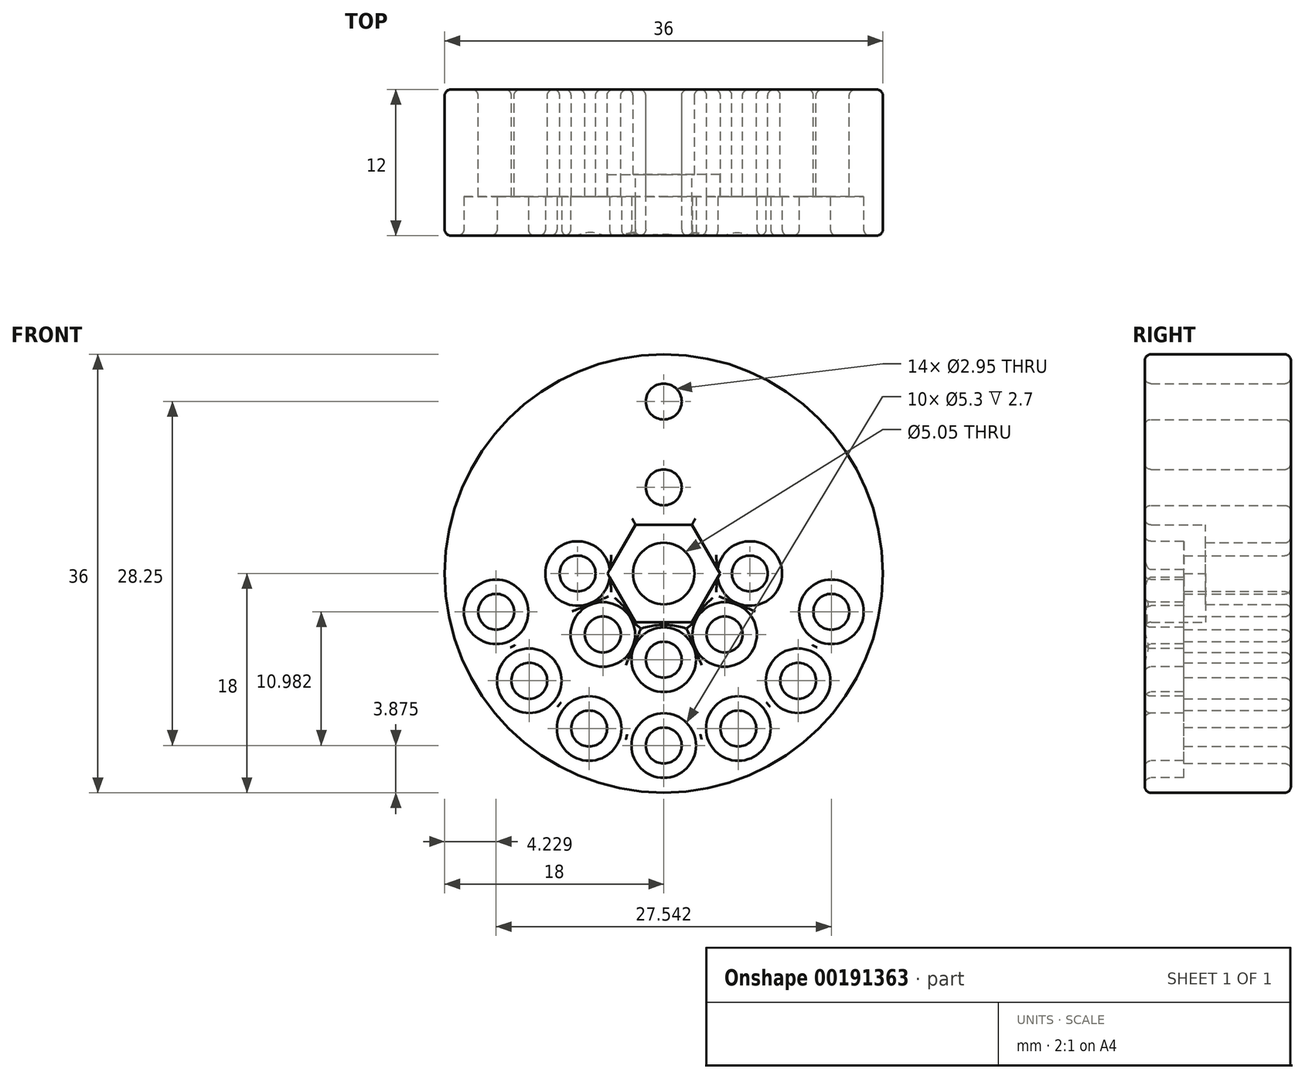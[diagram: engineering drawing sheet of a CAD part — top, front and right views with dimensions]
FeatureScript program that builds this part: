
annotation { "Feature Type Name" : "Feature", "Feature Type Description" : "" }
export const myFeature = defineFeature(function(context is Context, id is Id, definition is map)
    precondition{}
    {
        {
            assignVariable(context, id + "F0", {"name" : "nut_depth_mm", "anyValue" : 5});
        }
        {
            assignVariable(context, id + "F1", {"name" : "flywheel_depth_mm", "anyValue" : 12});
        }
        {
            var Q0;
            Q0=qCreatedBy(makeId("Front.planeOp"),FACE);
            var sketch = newSketch(context, id + "F2", { "sketchPlane" : qUnion([Q0])});
            skCircle(sketch, "E0", {"center": v(0, 0) * mm, "radius": 18 * mm});
            skCircle(sketch, "E1", {"center": v(0, 14.13) * mm, "radius": 1.48 * mm});
            skCircle(sketch, "E2.1.0", {"center": v(-6.13, 12.73) * mm, "radius": 1.48 * mm});
            skCircle(sketch, "E2.2.0", {"center": v(-11.04, 8.8) * mm, "radius": 1.47 * mm});
            skCircle(sketch, "E3.1.3.0", {"center": v(-13.77, 3.14) * mm, "radius": 1.48 * mm});
            skCircle(sketch, "E3.1.4.0", {"center": v(-13.77, -3.14) * mm, "radius": 1.48 * mm});
            skCircle(sketch, "E3.1.5.0", {"center": v(-11.04, -8.8) * mm, "radius": 1.47 * mm});
            skCircle(sketch, "E3.1.6.0", {"center": v(-6.13, -12.73) * mm, "radius": 1.47 * mm});
            skCircle(sketch, "E3.1.7.0", {"center": v(0, -14.13) * mm, "radius": 1.48 * mm});
            skCircle(sketch, "E3.1.8.0", {"center": v(6.13, -12.73) * mm, "radius": 1.47 * mm});
            skCircle(sketch, "E3.1.9.0", {"center": v(11.04, -8.8) * mm, "radius": 1.48 * mm});
            skCircle(sketch, "E3.1.10.0", {"center": v(13.77, -3.14) * mm, "radius": 1.48 * mm});
            skCircle(sketch, "E3.1.11.0", {"center": v(13.77, 3.14) * mm, "radius": 1.48 * mm});
            skCircle(sketch, "E3.1.12.0", {"center": v(11.04, 8.8) * mm, "radius": 1.48 * mm});
            skCircle(sketch, "E3.1.13.0", {"center": v(6.13, 12.73) * mm, "radius": 1.48 * mm});
            skCircle(sketch, "E4", {"center": v(0, 0) * mm, "radius": 2.5 * mm, "construction": true});
            skCircle(sketch, "E5", {"center": v(0, 0) * mm, "radius": 5.75 * mm, "construction": true});
            skCircle(sketch, "E6", {"center": v(0, 7.08) * mm, "radius": 1.48 * mm});
            skCircle(sketch, "E7.1.0", {"center": v(-5, 5) * mm, "radius": 1.48 * mm});
            skCircle(sketch, "E7.2.0", {"center": v(-7.08, 0) * mm, "radius": 1.48 * mm});
            skCircle(sketch, "E8.1.3.0", {"center": v(-5, -5) * mm, "radius": 1.48 * mm});
            skCircle(sketch, "E8.1.4.0", {"center": v(0, -7.08) * mm, "radius": 1.48 * mm});
            skCircle(sketch, "E8.1.5.0", {"center": v(5, -5) * mm, "radius": 1.48 * mm});
            skCircle(sketch, "E8.1.6.0", {"center": v(7.08, 0) * mm, "radius": 1.48 * mm});
            skCircle(sketch, "E8.1.7.0", {"center": v(5, 5) * mm, "radius": 1.48 * mm});
            skCircle(sketch, "E9.cCircle", {"center": v(0, 0) * mm, "radius": 4 * mm, "construction": true});
            skLineSegment(sketch, "E9.0", {"start": v(-2.3, 4) * mm, "end": v(2.3, 4) * mm});
            skLineSegment(sketch, "E9.1", {"start": v(2.3, 4) * mm, "end": v(4.62, 0) * mm});
            skLineSegment(sketch, "E9.2", {"start": v(4.62, 0) * mm, "end": v(2.3, -4) * mm});
            skLineSegment(sketch, "E9.3", {"start": v(2.3, -4) * mm, "end": v(-2.3, -4) * mm});
            skLineSegment(sketch, "E9.4", {"start": v(-2.3, -4) * mm, "end": v(-4.62, 0) * mm});
            skLineSegment(sketch, "E9.5", {"start": v(-4.62, 0) * mm, "end": v(-2.3, 4) * mm});
            skPoint(sketch, "E9.0.midPoint", {"position": v(0, 4) * mm});
            skSolve(sketch);
        }
        {
            var Q0;
            {var subQ0=sQuery(id+"F2.wireOp",EDGE,"E9.3");var subQ1=sQuery(id+"F2.wireOp",EDGE,"E5");var subQ2=makeQuery(id+"F2.imprint","INTERSECT",VERTEX,{"disambiguationData":[OD(0.0)],"derivedFrom":[subQ1,subQ0]});Q0=makeQuery(id+"F2.imprint","IMPRINT",FACE,{"disambiguationData":[TD([[makeQuery(id+"F2.imprint","IMPRINT",EDGE,{"disambiguationData":[TD([[subQ2,-1.0]])],"derivedFrom":subQ1}),1.0]])]});}
            var Q1;
            {var subQ0=sQuery(id+"F2.wireOp",EDGE,"E9.2");var subQ1=sQuery(id+"F2.wireOp",EDGE,"E5");var subQ2=makeQuery(id+"F2.imprint","INTERSECT",VERTEX,{"disambiguationData":[OD(0.0)],"derivedFrom":[subQ1,subQ0]});Q1=makeQuery(id+"F2.imprint","IMPRINT",FACE,{"disambiguationData":[TD([[makeQuery(id+"F2.imprint","IMPRINT",EDGE,{"disambiguationData":[TD([[subQ2,-1.0]])],"derivedFrom":subQ1}),1.0]])]});}
            var Q2;
            {var subQ0=sQuery(id+"F2.wireOp",EDGE,"E9.4");var subQ1=sQuery(id+"F2.wireOp",EDGE,"E5");var subQ2=makeQuery(id+"F2.imprint","INTERSECT",VERTEX,{"disambiguationData":[OD(0.0)],"derivedFrom":[subQ1,subQ0]});Q2=makeQuery(id+"F2.imprint","IMPRINT",FACE,{"disambiguationData":[TD([[makeQuery(id+"F2.imprint","IMPRINT",EDGE,{"disambiguationData":[TD([[subQ2,-1.0]])],"derivedFrom":subQ1}),1.0]])]});}
            var Q3;
            {var subQ0=sQuery(id+"F2.wireOp",EDGE,"E9.0");var subQ1=sQuery(id+"F2.wireOp",EDGE,"E5");var subQ2=makeQuery(id+"F2.imprint","INTERSECT",VERTEX,{"disambiguationData":[OD(0.0)],"derivedFrom":[subQ1,subQ0]});Q3=makeQuery(id+"F2.imprint","IMPRINT",FACE,{"disambiguationData":[TD([[makeQuery(id+"F2.imprint","IMPRINT",EDGE,{"disambiguationData":[TD([[subQ2,-1.0]])],"derivedFrom":subQ1}),1.0]])]});}
            var Q4;
            {var subQ0=sQuery(id+"F2.wireOp",EDGE,"E9.1");var subQ1=sQuery(id+"F2.wireOp",EDGE,"E5");var subQ2=makeQuery(id+"F2.imprint","INTERSECT",VERTEX,{"disambiguationData":[OD(0.0)],"derivedFrom":[subQ1,subQ0]});Q4=makeQuery(id+"F2.imprint","IMPRINT",FACE,{"disambiguationData":[TD([[makeQuery(id+"F2.imprint","IMPRINT",EDGE,{"disambiguationData":[TD([[subQ2,1.0]])],"derivedFrom":subQ1}),1.0]])]});}
            var Q5;
            Q5=makeQuery(id+"F2.imprint","IMPRINT",FACE,{"disambiguationData":[TD([[makeQuery(id+"F2.imprint","IMPRINT",EDGE,{"derivedFrom":sQuery(id+"F2.wireOp",EDGE,"E0")}),1.0]])]});
            var Q6;
            {var subQ0=sQuery(id+"F2.wireOp",EDGE,"E9.5");var subQ1=sQuery(id+"F2.wireOp",EDGE,"E5");var subQ2=makeQuery(id+"F2.imprint","INTERSECT",VERTEX,{"disambiguationData":[OD(0.0)],"derivedFrom":[subQ1,subQ0]});Q6=makeQuery(id+"F2.imprint","IMPRINT",FACE,{"disambiguationData":[TD([[makeQuery(id+"F2.imprint","IMPRINT",EDGE,{"disambiguationData":[TD([[subQ2,-1.0]])],"derivedFrom":subQ1}),1.0]])]});}
            var Q7;
            Q7=makeQuery(id+"F2.imprint","IMPRINT",FACE,{"disambiguationData":[TD([[makeQuery(id+"F2.imprint","IMPRINT",EDGE,{"derivedFrom":sQuery(id+"F2.wireOp",EDGE,"E3.1.13.0")}),1.0]])]});
            var Q8;
            Q8=makeQuery(id+"F2.imprint","IMPRINT",FACE,{"disambiguationData":[TD([[makeQuery(id+"F2.imprint","IMPRINT",EDGE,{"derivedFrom":sQuery(id+"F2.wireOp",EDGE,"E3.1.12.0")}),1.0]])]});
            var Q9;
            Q9=makeQuery(id+"F2.imprint","IMPRINT",FACE,{"disambiguationData":[TD([[makeQuery(id+"F2.imprint","IMPRINT",EDGE,{"derivedFrom":sQuery(id+"F2.wireOp",EDGE,"E3.1.11.0")}),1.0]])]});
            var Q10;
            Q10=makeQuery(id+"F2.imprint","IMPRINT",FACE,{"disambiguationData":[TD([[makeQuery(id+"F2.imprint","IMPRINT",EDGE,{"derivedFrom":sQuery(id+"F2.wireOp",EDGE,"E8.1.7.0")}),1.0]])]});
            var Q11;
            Q11=makeQuery(id+"F2.imprint","IMPRINT",FACE,{"disambiguationData":[TD([[makeQuery(id+"F2.imprint","IMPRINT",EDGE,{"derivedFrom":sQuery(id+"F2.wireOp",EDGE,"E7.1.0")}),1.0]])]});
            var Q12;
            Q12=makeQuery(id+"F2.imprint","IMPRINT",FACE,{"disambiguationData":[TD([[makeQuery(id+"F2.imprint","IMPRINT",EDGE,{"derivedFrom":sQuery(id+"F2.wireOp",EDGE,"E2.1.0")}),1.0]])]});
            var Q13;
            Q13=makeQuery(id+"F2.imprint","IMPRINT",FACE,{"disambiguationData":[TD([[makeQuery(id+"F2.imprint","IMPRINT",EDGE,{"derivedFrom":sQuery(id+"F2.wireOp",EDGE,"E2.2.0")}),1.0]])]});
            var Q14;
            Q14=makeQuery(id+"F2.imprint","IMPRINT",FACE,{"disambiguationData":[TD([[makeQuery(id+"F2.imprint","IMPRINT",EDGE,{"derivedFrom":sQuery(id+"F2.wireOp",EDGE,"E3.1.3.0")}),1.0]])]});
            extrude(context, id + "F3", {"entities" : qUnion([Q0, Q1, Q2, Q3, Q4, Q5, Q6, Q7, Q8, Q9, Q10, Q11, Q12, Q13, Q14]), "depth" : (getVariable(context, 'flywheel_depth_mm')) * mm});
        }
        {
            var Q0;
            Q0=makeQuery(id+"F2.imprint","IMPRINT",FACE,{"disambiguationData":[TD([[makeQuery(id+"F2.imprint","IMPRINT",EDGE,{"derivedFrom":sQuery(id+"F2.wireOp",EDGE,"E9.0")}),-1.0]])]});
            extrude(context, id + "F4", {"entities" : qUnion([Q0]), "operationType" : NewBodyOperationType.ADD, "depth" : (getVariable(context, 'flywheel_depth_mm') - getVariable(context, 'nut_depth_mm')) * mm});
        }
        {
            var Q0;
            Q0=sQuery(id+"F2.wireOp",VERTEX,"E0.center");
            var Q1;
            Q1=makeQuery(id+"F3.opExtrude","SWEPT_BODY",BODY,{"disambiguationData":[OSD([sQuery(id+"F2.wireOp",EDGE,"E0"),sQuery(id+"F2.wireOp",EDGE,"E1"),sQuery(id+"F2.wireOp",EDGE,"E2.1.0"),sQuery(id+"F2.wireOp",EDGE,"E2.2.0"),sQuery(id+"F2.wireOp",EDGE,"E3.1.3.0"),sQuery(id+"F2.wireOp",EDGE,"E3.1.4.0"),sQuery(id+"F2.wireOp",EDGE,"E3.1.5.0"),sQuery(id+"F2.wireOp",EDGE,"E3.1.6.0"),sQuery(id+"F2.wireOp",EDGE,"E3.1.7.0"),sQuery(id+"F2.wireOp",EDGE,"E3.1.8.0"),sQuery(id+"F2.wireOp",EDGE,"E3.1.9.0"),sQuery(id+"F2.wireOp",EDGE,"E3.1.10.0"),sQuery(id+"F2.wireOp",EDGE,"E3.1.11.0"),sQuery(id+"F2.wireOp",EDGE,"E3.1.12.0"),sQuery(id+"F2.wireOp",EDGE,"E3.1.13.0"),sQuery(id+"F2.wireOp",EDGE,"E3.1.14.0"),sQuery(id+"F2.wireOp",EDGE,"E3.1.15.0"),sQuery(id+"F2.wireOp",EDGE,"E6"),sQuery(id+"F2.wireOp",EDGE,"E7.1.0"),sQuery(id+"F2.wireOp",EDGE,"E7.2.0"),sQuery(id+"F2.wireOp",EDGE,"E8.1.3.0"),sQuery(id+"F2.wireOp",EDGE,"E8.1.4.0"),sQuery(id+"F2.wireOp",EDGE,"E8.1.5.0"),sQuery(id+"F2.wireOp",EDGE,"E8.1.6.0"),sQuery(id+"F2.wireOp",EDGE,"E8.1.7.0"),sQuery(id+"F2.wireOp",EDGE,"E9.0"),sQuery(id+"F2.wireOp",EDGE,"E9.1"),sQuery(id+"F2.wireOp",EDGE,"E9.2"),sQuery(id+"F2.wireOp",EDGE,"E9.3"),sQuery(id+"F2.wireOp",EDGE,"E9.4"),sQuery(id+"F2.wireOp",EDGE,"E9.5")])]});
            hole(context, id + "F5", {"style" : HoleStyle.SIMPLE, "endStyle" : HoleEndStyle.THROUGH, "oppositeDirection" : true, "holeDiameter" : 5.05 * mm, "tappedDepth" : 12 * mm, "tapClearance" : 3, "locations" : qUnion([Q0]), "scope" : qUnion([Q1])});
        }
        {
            var Q0;
            Q0=makeQuery(id+"F3.opExtrude","CAP_FACE",FACE,{"disambiguationData":[OSD([sQuery(id+"F2.wireOp",EDGE,"E0"),sQuery(id+"F2.wireOp",EDGE,"E1"),sQuery(id+"F2.wireOp",EDGE,"E2.1.0"),sQuery(id+"F2.wireOp",EDGE,"E2.2.0"),sQuery(id+"F2.wireOp",EDGE,"E3.1.3.0"),sQuery(id+"F2.wireOp",EDGE,"E3.1.4.0"),sQuery(id+"F2.wireOp",EDGE,"E3.1.5.0"),sQuery(id+"F2.wireOp",EDGE,"E3.1.6.0"),sQuery(id+"F2.wireOp",EDGE,"E3.1.7.0"),sQuery(id+"F2.wireOp",EDGE,"E3.1.8.0"),sQuery(id+"F2.wireOp",EDGE,"E3.1.9.0"),sQuery(id+"F2.wireOp",EDGE,"E3.1.10.0"),sQuery(id+"F2.wireOp",EDGE,"E3.1.11.0"),sQuery(id+"F2.wireOp",EDGE,"E3.1.12.0"),sQuery(id+"F2.wireOp",EDGE,"E3.1.13.0"),sQuery(id+"F2.wireOp",EDGE,"E3.1.14.0"),sQuery(id+"F2.wireOp",EDGE,"E3.1.15.0"),sQuery(id+"F2.wireOp",EDGE,"E6"),sQuery(id+"F2.wireOp",EDGE,"E7.1.0"),sQuery(id+"F2.wireOp",EDGE,"E7.2.0"),sQuery(id+"F2.wireOp",EDGE,"E8.1.3.0"),sQuery(id+"F2.wireOp",EDGE,"E8.1.4.0"),sQuery(id+"F2.wireOp",EDGE,"E8.1.5.0"),sQuery(id+"F2.wireOp",EDGE,"E8.1.6.0"),sQuery(id+"F2.wireOp",EDGE,"E8.1.7.0"),sQuery(id+"F2.wireOp",EDGE,"E9.0"),sQuery(id+"F2.wireOp",EDGE,"E9.1"),sQuery(id+"F2.wireOp",EDGE,"E9.2"),sQuery(id+"F2.wireOp",EDGE,"E9.3"),sQuery(id+"F2.wireOp",EDGE,"E9.4"),sQuery(id+"F2.wireOp",EDGE,"E9.5")])],"isStart":false});
            var sketch = newSketch(context, id + "F6", { "sketchPlane" : qUnion([Q0])});
            skCircle(sketch, "E10", {"center": v(-7.08, 0) * mm, "radius": 2.65 * mm});
            skCircle(sketch, "E11", {"center": v(-13.77, -3.14) * mm, "radius": 2.65 * mm});
            skCircle(sketch, "E12", {"center": v(-11.04, -8.8) * mm, "radius": 2.65 * mm});
            skCircle(sketch, "E13", {"center": v(-5, -5) * mm, "radius": 2.65 * mm});
            skCircle(sketch, "E14", {"center": v(-6.13, -12.73) * mm, "radius": 2.65 * mm});
            skCircle(sketch, "E15", {"center": v(0, -14.13) * mm, "radius": 2.65 * mm});
            skCircle(sketch, "E16", {"center": v(6.13, -12.73) * mm, "radius": 2.65 * mm});
            skCircle(sketch, "E17", {"center": v(0, -7.08) * mm, "radius": 2.65 * mm});
            skCircle(sketch, "E18", {"center": v(11.04, -8.8) * mm, "radius": 2.65 * mm});
            skCircle(sketch, "E19", {"center": v(13.77, -3.14) * mm, "radius": 2.65 * mm});
            skCircle(sketch, "E20", {"center": v(5, -5) * mm, "radius": 2.65 * mm});
            skCircle(sketch, "E21", {"center": v(7.08, 0) * mm, "radius": 2.65 * mm});
            skSolve(sketch);
        }
        {
            var Q0;
            Q0=makeQuery(id+"F6.imprint","IMPRINT",FACE,{"disambiguationData":[TD([[makeQuery(id+"F6.imprint","IMPRINT",EDGE,{"derivedFrom":sQuery(id+"F6.wireOp",EDGE,"E13")}),1.0]])]});
            var Q1;
            Q1=makeQuery(id+"F6.imprint","IMPRINT",FACE,{"disambiguationData":[TD([[makeQuery(id+"F6.imprint","IMPRINT",EDGE,{"derivedFrom":makeQuery(id+"F3.opExtrude","CAP_EDGE",EDGE,{"disambiguationData":[OSD([sQuery(id+"F2.wireOp",EDGE,"E7.2.0")])],"isStart":false})}),-1.0]])]});
            var Q2;
            Q2=makeQuery(id+"F6.imprint","IMPRINT",FACE,{"disambiguationData":[TD([[makeQuery(id+"F6.imprint","IMPRINT",EDGE,{"derivedFrom":sQuery(id+"F6.wireOp",EDGE,"E11")}),1.0]])]});
            var Q3;
            Q3=makeQuery(id+"F6.imprint","IMPRINT",FACE,{"disambiguationData":[TD([[makeQuery(id+"F6.imprint","IMPRINT",EDGE,{"derivedFrom":sQuery(id+"F6.wireOp",EDGE,"E12")}),1.0]])]});
            var Q4;
            Q4=makeQuery(id+"F6.imprint","IMPRINT",FACE,{"disambiguationData":[TD([[makeQuery(id+"F6.imprint","IMPRINT",EDGE,{"derivedFrom":sQuery(id+"F6.wireOp",EDGE,"E14")}),1.0]])]});
            var Q5;
            Q5=makeQuery(id+"F6.imprint","IMPRINT",FACE,{"disambiguationData":[TD([[makeQuery(id+"F6.imprint","IMPRINT",EDGE,{"derivedFrom":sQuery(id+"F6.wireOp",EDGE,"E17")}),1.0]])]});
            var Q6;
            Q6=makeQuery(id+"F6.imprint","IMPRINT",FACE,{"disambiguationData":[TD([[makeQuery(id+"F6.imprint","IMPRINT",EDGE,{"derivedFrom":sQuery(id+"F6.wireOp",EDGE,"E20")}),1.0]])]});
            var Q7;
            Q7=makeQuery(id+"F6.imprint","IMPRINT",FACE,{"disambiguationData":[TD([[makeQuery(id+"F6.imprint","IMPRINT",EDGE,{"derivedFrom":makeQuery(id+"F3.opExtrude","CAP_EDGE",EDGE,{"disambiguationData":[OSD([sQuery(id+"F2.wireOp",EDGE,"E8.1.6.0")])],"isStart":false})}),-1.0]])]});
            var Q8;
            Q8=makeQuery(id+"F6.imprint","IMPRINT",FACE,{"disambiguationData":[TD([[makeQuery(id+"F6.imprint","IMPRINT",EDGE,{"derivedFrom":sQuery(id+"F6.wireOp",EDGE,"E19")}),1.0]])]});
            var Q9;
            Q9=makeQuery(id+"F6.imprint","IMPRINT",FACE,{"disambiguationData":[TD([[makeQuery(id+"F6.imprint","IMPRINT",EDGE,{"derivedFrom":sQuery(id+"F6.wireOp",EDGE,"E18")}),1.0]])]});
            var Q10;
            Q10=makeQuery(id+"F6.imprint","IMPRINT",FACE,{"disambiguationData":[TD([[makeQuery(id+"F6.imprint","IMPRINT",EDGE,{"derivedFrom":sQuery(id+"F6.wireOp",EDGE,"E16")}),1.0]])]});
            var Q11;
            Q11=makeQuery(id+"F6.imprint","IMPRINT",FACE,{"disambiguationData":[TD([[makeQuery(id+"F6.imprint","IMPRINT",EDGE,{"derivedFrom":sQuery(id+"F6.wireOp",EDGE,"E15")}),1.0]])]});
            extrude(context, id + "F7", {"entities" : qUnion([Q0, Q1, Q2, Q3, Q4, Q5, Q6, Q7, Q8, Q9, Q10, Q11]), "operationType" : NewBodyOperationType.REMOVE, "oppositeDirection" : true, "depth" : 3.2 * mm});
        }
        {
            var Q0;
            Q0=makeQuery(id+"F3.opExtrude","CAP_EDGE",EDGE,{"disambiguationData":[OSD([sQuery(id+"F2.wireOp",EDGE,"E9.0")])],"isStart":false});
            var Q1;
            Q1=makeQuery(id+"F3.opExtrude","CAP_EDGE",EDGE,{"disambiguationData":[OSD([sQuery(id+"F2.wireOp",EDGE,"E9.1")])],"isStart":false});
            var Q2;
            Q2=makeQuery(id+"F3.opExtrude","CAP_EDGE",EDGE,{"disambiguationData":[OSD([sQuery(id+"F2.wireOp",EDGE,"E9.2")])],"isStart":false});
            var Q3;
            Q3=makeQuery(id+"F3.opExtrude","CAP_EDGE",EDGE,{"disambiguationData":[OSD([sQuery(id+"F2.wireOp",EDGE,"E9.3")])],"isStart":false});
            var Q4;
            Q4=makeQuery(id+"F3.opExtrude","CAP_EDGE",EDGE,{"disambiguationData":[OSD([sQuery(id+"F2.wireOp",EDGE,"E9.4")])],"isStart":false});
            var Q5;
            Q5=makeQuery(id+"F3.opExtrude","CAP_EDGE",EDGE,{"disambiguationData":[OSD([sQuery(id+"F2.wireOp",EDGE,"E9.5")])],"isStart":false});
            var Q6;
            Q6=makeQuery(id+"F3.opExtrude","CAP_EDGE",EDGE,{"disambiguationData":[OSD([sQuery(id+"F2.wireOp",EDGE,"E0")])],"isStart":false});
            var Q7;
            Q7=makeQuery(id+"F3.opExtrude","CAP_EDGE",EDGE,{"disambiguationData":[OSD([sQuery(id+"F2.wireOp",EDGE,"E0")])],"isStart":true});
            var Q8;
            Q8=makeQuery(id+"F4.opExtrude","CAP_EDGE",EDGE,{"disambiguationData":[OSD([sQuery(id+"F2.wireOp",EDGE,"E4")])],"isStart":true});
            var Q9;
            Q9=makeQuery(id+"F4.opExtrude","CAP_EDGE",EDGE,{"disambiguationData":[OSD([sQuery(id+"F2.wireOp",EDGE,"E4")])],"isStart":false});
            var Q10;
            Q10=makeQuery(id+"F3.opExtrude","CAP_FACE",FACE,{"disambiguationData":[OSD([sQuery(id+"F2.wireOp",EDGE,"E0"),sQuery(id+"F2.wireOp",EDGE,"E1"),sQuery(id+"F2.wireOp",EDGE,"E2.1.0"),sQuery(id+"F2.wireOp",EDGE,"E2.2.0"),sQuery(id+"F2.wireOp",EDGE,"E3.1.3.0"),sQuery(id+"F2.wireOp",EDGE,"E3.1.4.0"),sQuery(id+"F2.wireOp",EDGE,"E3.1.5.0"),sQuery(id+"F2.wireOp",EDGE,"E3.1.6.0"),sQuery(id+"F2.wireOp",EDGE,"E3.1.7.0"),sQuery(id+"F2.wireOp",EDGE,"E3.1.8.0"),sQuery(id+"F2.wireOp",EDGE,"E3.1.9.0"),sQuery(id+"F2.wireOp",EDGE,"E3.1.10.0"),sQuery(id+"F2.wireOp",EDGE,"E3.1.11.0"),sQuery(id+"F2.wireOp",EDGE,"E3.1.12.0"),sQuery(id+"F2.wireOp",EDGE,"E3.1.13.0"),sQuery(id+"F2.wireOp",EDGE,"E3.1.14.0"),sQuery(id+"F2.wireOp",EDGE,"E3.1.15.0"),sQuery(id+"F2.wireOp",EDGE,"E6"),sQuery(id+"F2.wireOp",EDGE,"E7.1.0"),sQuery(id+"F2.wireOp",EDGE,"E7.2.0"),sQuery(id+"F2.wireOp",EDGE,"E8.1.3.0"),sQuery(id+"F2.wireOp",EDGE,"E8.1.4.0"),sQuery(id+"F2.wireOp",EDGE,"E8.1.5.0"),sQuery(id+"F2.wireOp",EDGE,"E8.1.6.0"),sQuery(id+"F2.wireOp",EDGE,"E8.1.7.0"),sQuery(id+"F2.wireOp",EDGE,"E9.0"),sQuery(id+"F2.wireOp",EDGE,"E9.1"),sQuery(id+"F2.wireOp",EDGE,"E9.2"),sQuery(id+"F2.wireOp",EDGE,"E9.3"),sQuery(id+"F2.wireOp",EDGE,"E9.4"),sQuery(id+"F2.wireOp",EDGE,"E9.5")])],"isStart":false});
            var Q11;
            {var subQ0=sQuery(id+"F2.wireOp",EDGE,"E9.5");var subQ1=sQuery(id+"F2.wireOp",EDGE,"E9.4");var subQ2=sQuery(id+"F2.wireOp",EDGE,"E9.3");var subQ3=sQuery(id+"F2.wireOp",EDGE,"E9.2");var subQ4=sQuery(id+"F2.wireOp",EDGE,"E9.1");var subQ5=sQuery(id+"F2.wireOp",EDGE,"E9.0");Q11=makeQuery(id+"F4.boolean.opBoolean","MERGE",FACE,{"derivedFrom":[makeQuery(id+"F3.opExtrude","CAP_FACE",FACE,{"disambiguationData":[OSD([sQuery(id+"F2.wireOp",EDGE,"E0"),sQuery(id+"F2.wireOp",EDGE,"E1"),sQuery(id+"F2.wireOp",EDGE,"E2.1.0"),sQuery(id+"F2.wireOp",EDGE,"E2.2.0"),sQuery(id+"F2.wireOp",EDGE,"E3.1.3.0"),sQuery(id+"F2.wireOp",EDGE,"E3.1.4.0"),sQuery(id+"F2.wireOp",EDGE,"E3.1.5.0"),sQuery(id+"F2.wireOp",EDGE,"E3.1.6.0"),sQuery(id+"F2.wireOp",EDGE,"E3.1.7.0"),sQuery(id+"F2.wireOp",EDGE,"E3.1.8.0"),sQuery(id+"F2.wireOp",EDGE,"E3.1.9.0"),sQuery(id+"F2.wireOp",EDGE,"E3.1.10.0"),sQuery(id+"F2.wireOp",EDGE,"E3.1.11.0"),sQuery(id+"F2.wireOp",EDGE,"E3.1.12.0"),sQuery(id+"F2.wireOp",EDGE,"E3.1.13.0"),sQuery(id+"F2.wireOp",EDGE,"E3.1.14.0"),sQuery(id+"F2.wireOp",EDGE,"E3.1.15.0"),sQuery(id+"F2.wireOp",EDGE,"E6"),sQuery(id+"F2.wireOp",EDGE,"E7.1.0"),sQuery(id+"F2.wireOp",EDGE,"E7.2.0"),sQuery(id+"F2.wireOp",EDGE,"E8.1.3.0"),sQuery(id+"F2.wireOp",EDGE,"E8.1.4.0"),sQuery(id+"F2.wireOp",EDGE,"E8.1.5.0"),sQuery(id+"F2.wireOp",EDGE,"E8.1.6.0"),sQuery(id+"F2.wireOp",EDGE,"E8.1.7.0"),subQ5,subQ4,subQ3,subQ2,subQ1,subQ0])],"isStart":true}),makeQuery(id+"F4.opExtrude","CAP_FACE",FACE,{"disambiguationData":[OSD([sQuery(id+"F2.wireOp",EDGE,"E4"),subQ5,subQ4,subQ3,subQ2,subQ1,subQ0])],"isStart":true})]});}
            var Q12;
            Q12=makeQuery(id+"F5.hole-0.boolean.opBoolean","INTERSECT",EDGE,{"derivedFrom":[makeQuery(id+"F4.opExtrude","CAP_FACE",FACE,{"disambiguationData":[OSD([sQuery(id+"F2.wireOp",EDGE,"E9.0"),sQuery(id+"F2.wireOp",EDGE,"E9.1"),sQuery(id+"F2.wireOp",EDGE,"E9.2"),sQuery(id+"F2.wireOp",EDGE,"E9.3"),sQuery(id+"F2.wireOp",EDGE,"E9.4"),sQuery(id+"F2.wireOp",EDGE,"E9.5")])],"isStart":false}),makeQuery(id+"F5.hole-0.opRevolve","SWEPT_FACE",FACE,{"disambiguationData":[OSD([sQuery(id+"F5.hole-0.sketch.wireOp",EDGE,"core_line_2")])]})]});
            fillet(context, id + "F8", {"entities" : qUnion([Q0, Q1, Q2, Q3, Q4, Q5, Q6, Q7, Q8, Q9, Q10, Q11, Q12]), "radius" : .5 * mm, "tangentPropagation" : true, "allowEdgeOverflow" : false});
        }
    });
